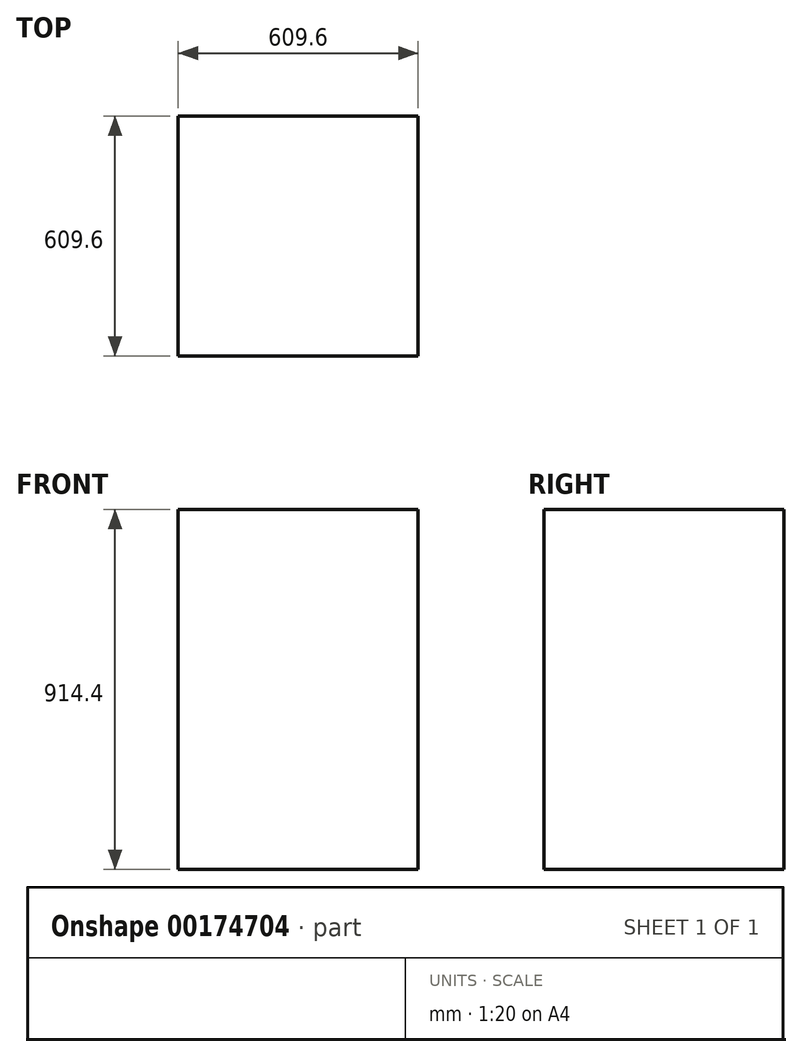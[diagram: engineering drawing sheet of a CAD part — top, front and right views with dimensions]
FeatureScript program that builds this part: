
annotation { "Feature Type Name" : "Feature", "Feature Type Description" : "" }
export const myFeature = defineFeature(function(context is Context, id is Id, definition is map)
    precondition{}
    {
        {
            var Q0;
            Q0=qCreatedBy(makeId("Top.planeOp"),FACE);
            var sketch = newSketch(context, id + "F0", { "sketchPlane" : qUnion([Q0])});
            skLineSegment(sketch, "E0.bottom", {"start": v(304.8, -304.8) * mm, "end": v(-304.8, -304.8) * mm});
            skLineSegment(sketch, "E0.top", {"start": v(304.8, 304.8) * mm, "end": v(-304.8, 304.8) * mm});
            skLineSegment(sketch, "E0.left", {"start": v(304.8, -304.8) * mm, "end": v(304.8, 304.8) * mm});
            skLineSegment(sketch, "E0.right", {"start": v(-304.8, -304.8) * mm, "end": v(-304.8, 304.8) * mm});
            skPoint(sketch, "E0.middle", {"position": v(0, 0) * mm});
            skSolve(sketch);
        }
        {
            var Q0;
            Q0 = qSketchRegion(id + "F0", true);
            extrude(context, id + "F1", {"entities" : qUnion([Q0]), "depth" : 914.4 * mm});
        }
    });
